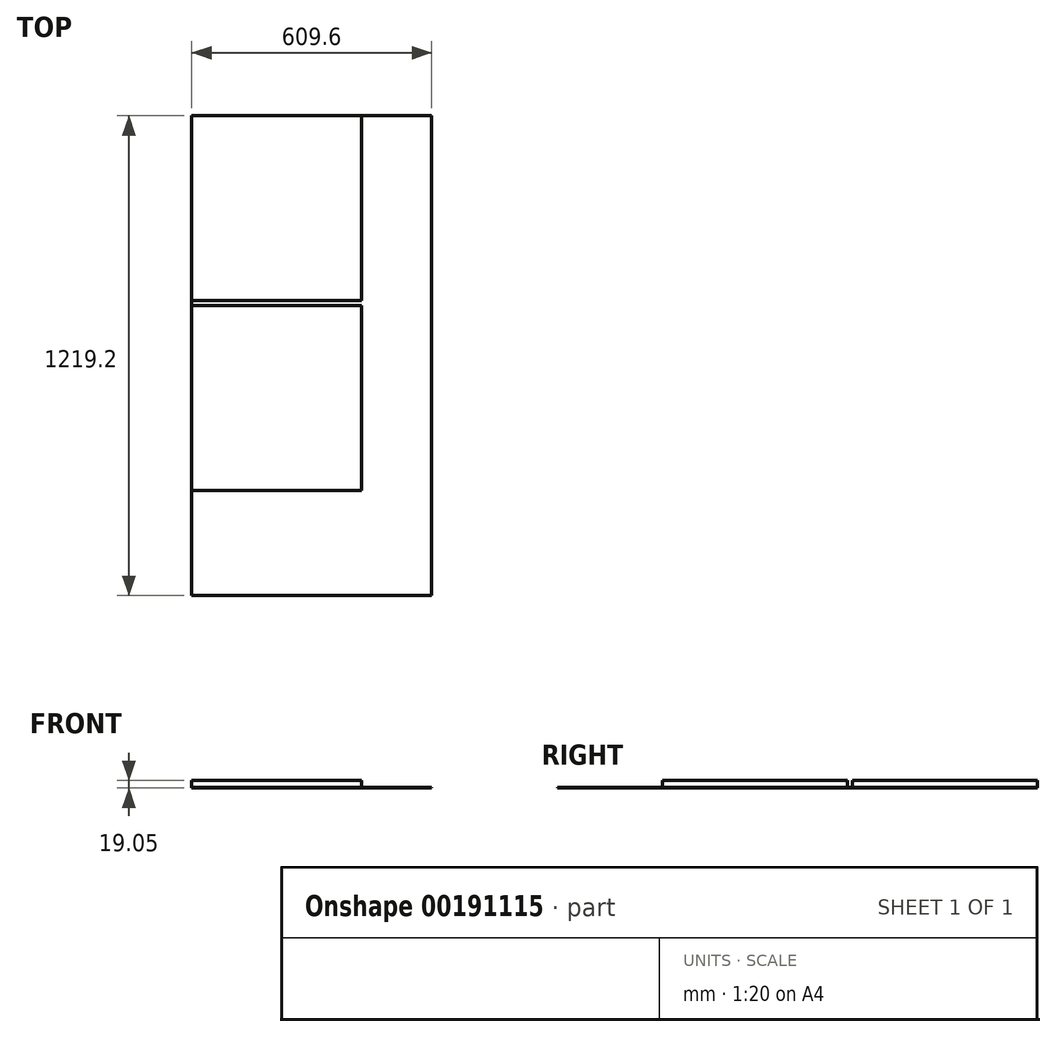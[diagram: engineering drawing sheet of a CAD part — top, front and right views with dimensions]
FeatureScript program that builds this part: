
annotation { "Feature Type Name" : "Feature", "Feature Type Description" : "" }
export const myFeature = defineFeature(function(context is Context, id is Id, definition is map)
    precondition{}
    {
        {
            var Q0;
            Q0=qCreatedBy(makeId("Top.planeOp"),FACE);
            var sketch = newSketch(context, id + "F0", { "sketchPlane" : qUnion([Q0])});
            skLineSegment(sketch, "E0.bottom", {"start": v(-304.8, 609.6) * mm, "end": v(304.8, 609.6) * mm});
            skLineSegment(sketch, "E0.top", {"start": v(-304.8, -609.6) * mm, "end": v(304.8, -609.6) * mm});
            skLineSegment(sketch, "E0.left", {"start": v(-304.8, 609.6) * mm, "end": v(-304.8, -609.6) * mm});
            skLineSegment(sketch, "E0.right", {"start": v(304.8, 609.6) * mm, "end": v(304.8, -609.6) * mm});
            skPoint(sketch, "E0.middle", {"position": v(0, 0) * mm});
            skSolve(sketch);
        }
        {
            var Q0;
            Q0 = qSketchRegion(id + "F0", true);
            extrude(context, id + "F1", {"entities" : qUnion([Q0]), "depth" : 19.05 * mm});
        }
        {
            var Q0;
            Q0=makeQuery(id+"F1.opExtrude","CAP_FACE",FACE,{"disambiguationData":[OSD([sQuery(id+"F0.wireOp",EDGE,"E0.bottom"),sQuery(id+"F0.wireOp",EDGE,"E0.top"),sQuery(id+"F0.wireOp",EDGE,"E0.left"),sQuery(id+"F0.wireOp",EDGE,"E0.right")])],"isStart":false});
            var sketch = newSketch(context, id + "F2", { "sketchPlane" : qUnion([Q0])});
            skLineSegment(sketch, "E1.bottom", {"start": v(-304.8, 609.6) * mm, "end": v(127, 609.6) * mm});
            skLineSegment(sketch, "E1.top", {"start": v(-304.8, 139.7) * mm, "end": v(127, 139.7) * mm});
            skLineSegment(sketch, "E1.left", {"start": v(-304.8, 609.6) * mm, "end": v(-304.8, 139.7) * mm});
            skLineSegment(sketch, "E1.right", {"start": v(127, 609.6) * mm, "end": v(127, 139.7) * mm});
            skLineSegment(sketch, "E2.bottom", {"start": v(-304.8, 127) * mm, "end": v(127, 127) * mm});
            skLineSegment(sketch, "E2.top", {"start": v(-304.8, -342.9) * mm, "end": v(127, -342.9) * mm});
            skLineSegment(sketch, "E2.left", {"start": v(-304.8, 127) * mm, "end": v(-304.8, -342.9) * mm});
            skLineSegment(sketch, "E2.right", {"start": v(127, 127) * mm, "end": v(127, -342.9) * mm});
            skSolve(sketch);
        }
        {
            var Q0;
            {var subQ7=sQuery(id+"F2.wireOp",EDGE,"E1.top");Q0=makeQuery(id+"F2.imprint","IMPRINT",FACE,{"disambiguationData":[TD([[makeQuery(id+"F2.imprint","IMPRINT",EDGE,{"derivedFrom":subQ7}),-1.0]])]});}
            extrude(context, id + "F3", {"entities" : qUnion([Q0]), "operationType" : NewBodyOperationType.REMOVE, "oppositeDirection" : true, "depth" : 17.14 * mm});
        }
    });
